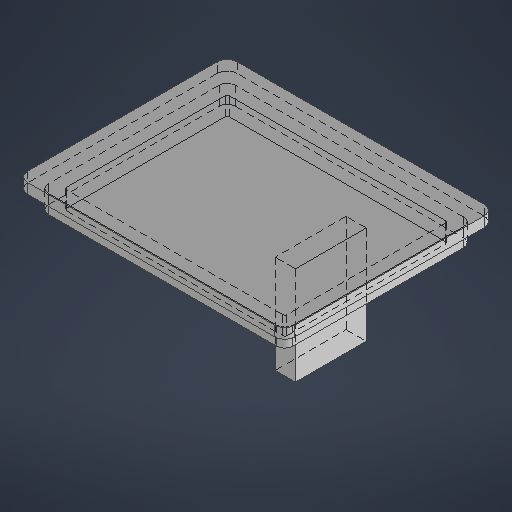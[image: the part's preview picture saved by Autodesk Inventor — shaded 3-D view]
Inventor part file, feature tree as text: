
AUTODESK INVENTOR PART (.ipt)
format: ipt  version: 2025.2 (Build 292293000, 293)  size: 215,040 bytes
history: native  units: mm
features: extrude x3, fillet x3, sketch x1
ambient origin geometry x8: Origin, YZ Plane, XZ Plane, XY Plane, X Axis, Y Axis, Z Axis, Center Point
bodies: Solid1 (feature_tree)
feature tree (7):
  sketch  "Sketch1"  dims[d0=5.0mm d1=0.0mm d2=9.0mm d3=0.0mm d4=48.5mm d5=0.0mm d6=5.0mm d7=4.0mm d8=1.0mm d9=0.5mm d10=6.0mm d11=10.0mm d12=35.0mm d13=24.0mm]
  extrude  "Extrusion1"  Depth=9.0mm TaperAngle=0.0deg
  extrude  "Extrusion2"  Depth=48.5mm TaperAngle=0.0deg
  extrude  "Extrusion3"  Depth=5.0mm
  fillet  "Fillet1"  Radius=4.0mm
  fillet  "Fillet2"  Radius=1.0mm
  fillet  "Fillet3"  Radius=0.5mm
